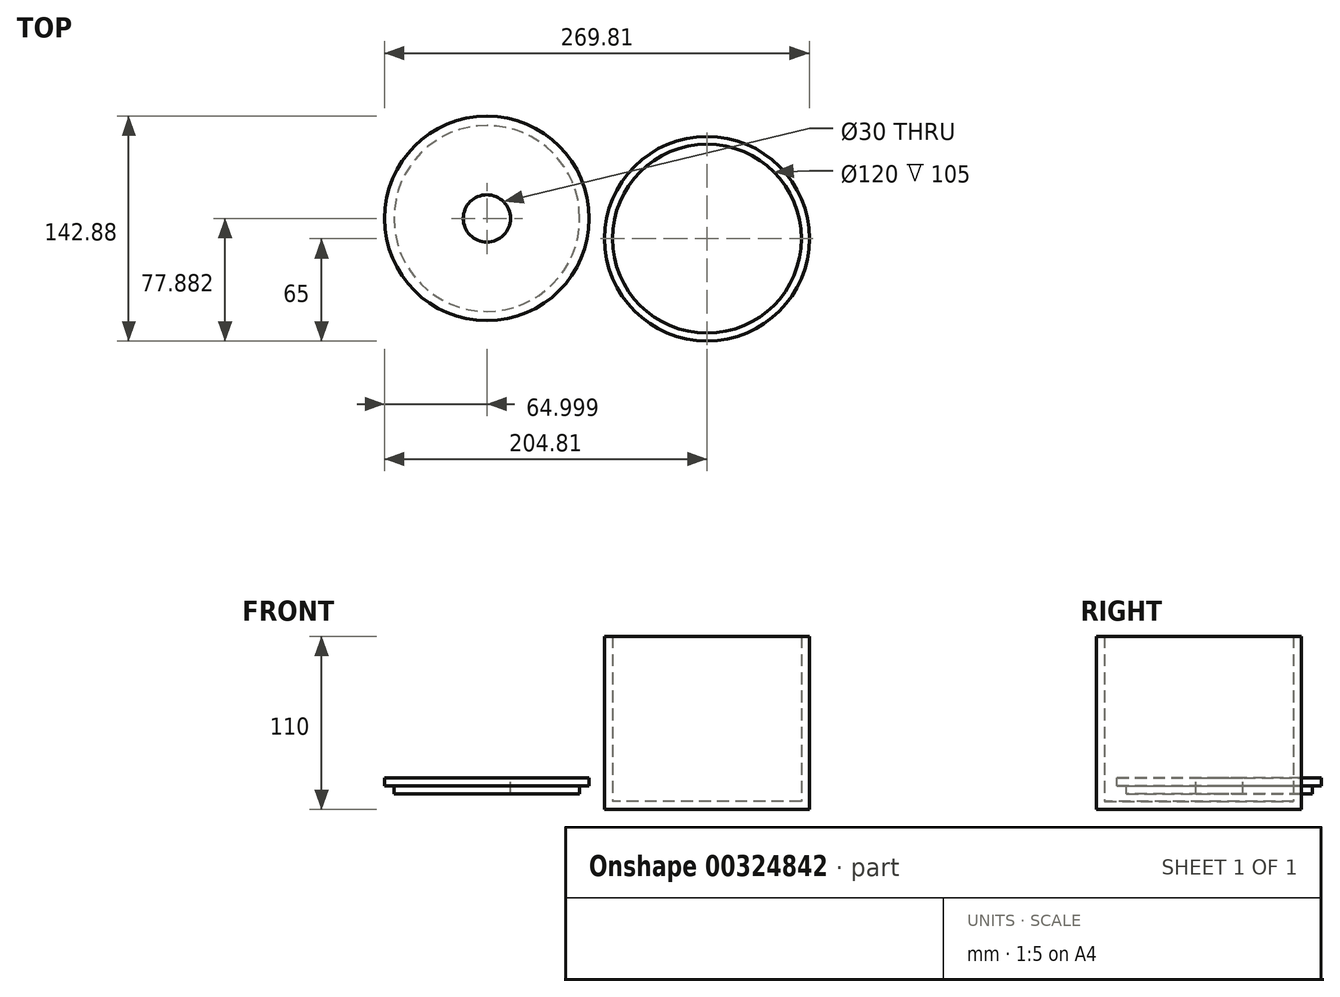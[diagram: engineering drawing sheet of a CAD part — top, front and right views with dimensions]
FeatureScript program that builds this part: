
annotation { "Feature Type Name" : "Feature", "Feature Type Description" : "" }
export const myFeature = defineFeature(function(context is Context, id is Id, definition is map)
    precondition{}
    {
        {
            var Q0;
            Q0=qCreatedBy(makeId("Top.planeOp"),FACE);
            var sketch = newSketch(context, id + "F0", { "sketchPlane" : qUnion([Q0])});
            skCircle(sketch, "E0", {"center": v(0, 0) * mm, "radius": 60 * mm});
            skCircle(sketch, "E1", {"center": v(0, 0) * mm, "radius": 65 * mm});
            skSolve(sketch);
        }
        {
            var Q0;
            Q0=makeQuery(id+"F0.imprint","IMPRINT",FACE,{"disambiguationData":[TD([[makeQuery(id+"F0.imprint","IMPRINT",EDGE,{"derivedFrom":sQuery(id+"F0.wireOp",EDGE,"E0")}),1.0]])]});
            extrude(context, id + "F1", {"entities" : qUnion([Q0]), "depth" : 5 * mm});
        }
        {
            var Q0;
            Q0=makeQuery(id+"F0.imprint","IMPRINT",FACE,{"disambiguationData":[TD([[makeQuery(id+"F0.imprint","IMPRINT",EDGE,{"derivedFrom":sQuery(id+"F0.wireOp",EDGE,"E0")}),-1.0]])]});
            extrude(context, id + "F2", {"entities" : qUnion([Q0]), "operationType" : NewBodyOperationType.ADD, "depth" : 110 * mm});
        }
        {
            var Q0;
            Q0=qCreatedBy(makeId("Top.planeOp"),FACE);
            var sketch = newSketch(context, id + "F3", { "sketchPlane" : qUnion([Q0])});
            skCircle(sketch, "E2", {"center": v(-139.81, 12.88) * mm, "radius": 59 * mm});
            skCircle(sketch, "E3", {"center": v(-139.81, 12.88) * mm, "radius": 65 * mm});
            skCircle(sketch, "E4", {"center": v(-139.81, 12.88) * mm, "radius": 15 * mm});
            skSolve(sketch);
        }
        {
            var Q0;
            Q0=makeQuery(id+"F3.imprint","IMPRINT",FACE,{"disambiguationData":[TD([[makeQuery(id+"F3.imprint","IMPRINT",EDGE,{"derivedFrom":sQuery(id+"F3.wireOp",EDGE,"E2")}),1.0]])]});
            extrude(context, id + "F4", {"entities" : qUnion([Q0]), "depth" : 10 * mm});
        }
        {
            var Q0;
            Q0=makeQuery(id+"F3.imprint","IMPRINT",FACE,{"disambiguationData":[TD([[makeQuery(id+"F3.imprint","IMPRINT",EDGE,{"derivedFrom":sQuery(id+"F3.wireOp",EDGE,"E2")}),-1.0]])]});
            extrude(context, id + "F5", {"entities" : qUnion([Q0]), "operationType" : NewBodyOperationType.ADD, "depth" : 5 * mm});
        }
        {
            var Q0;
            Q0=makeQuery(id+"F4.opExtrude","CAP_FACE",FACE,{"disambiguationData":[OSD([sQuery(id+"F3.wireOp",EDGE,"E2"),sQuery(id+"F3.wireOp",EDGE,"E4")])],"isStart":false});
            var sketch = newSketch(context, id + "F6", { "sketchPlane" : qUnion([Q0])});
            skLineSegment(sketch, "E5", {"start": v(-139.81, 12.88) * mm, "end": v(-216.64, 12.88) * mm, "construction": true});
            skSolve(sketch);
        }
        {
            var Q0;
            Q0=makeQuery(id+"F4.opExtrude","SWEPT_BODY",BODY,{"disambiguationData":[OSD([sQuery(id+"F3.wireOp",EDGE,"E2"),sQuery(id+"F3.wireOp",EDGE,"E4")])]});
            var Q1;
            Q1=sQuery(id+"F6.wireOp",EDGE,"E5");
            transform(context, id + "F7", {"entities" : qUnion([Q0]), "transformType" : TransformType.ROTATION, "transformAxis" : qUnion([Q1]), "angle" : 180 * degree, "makeCopy" : false});
        }
    });
